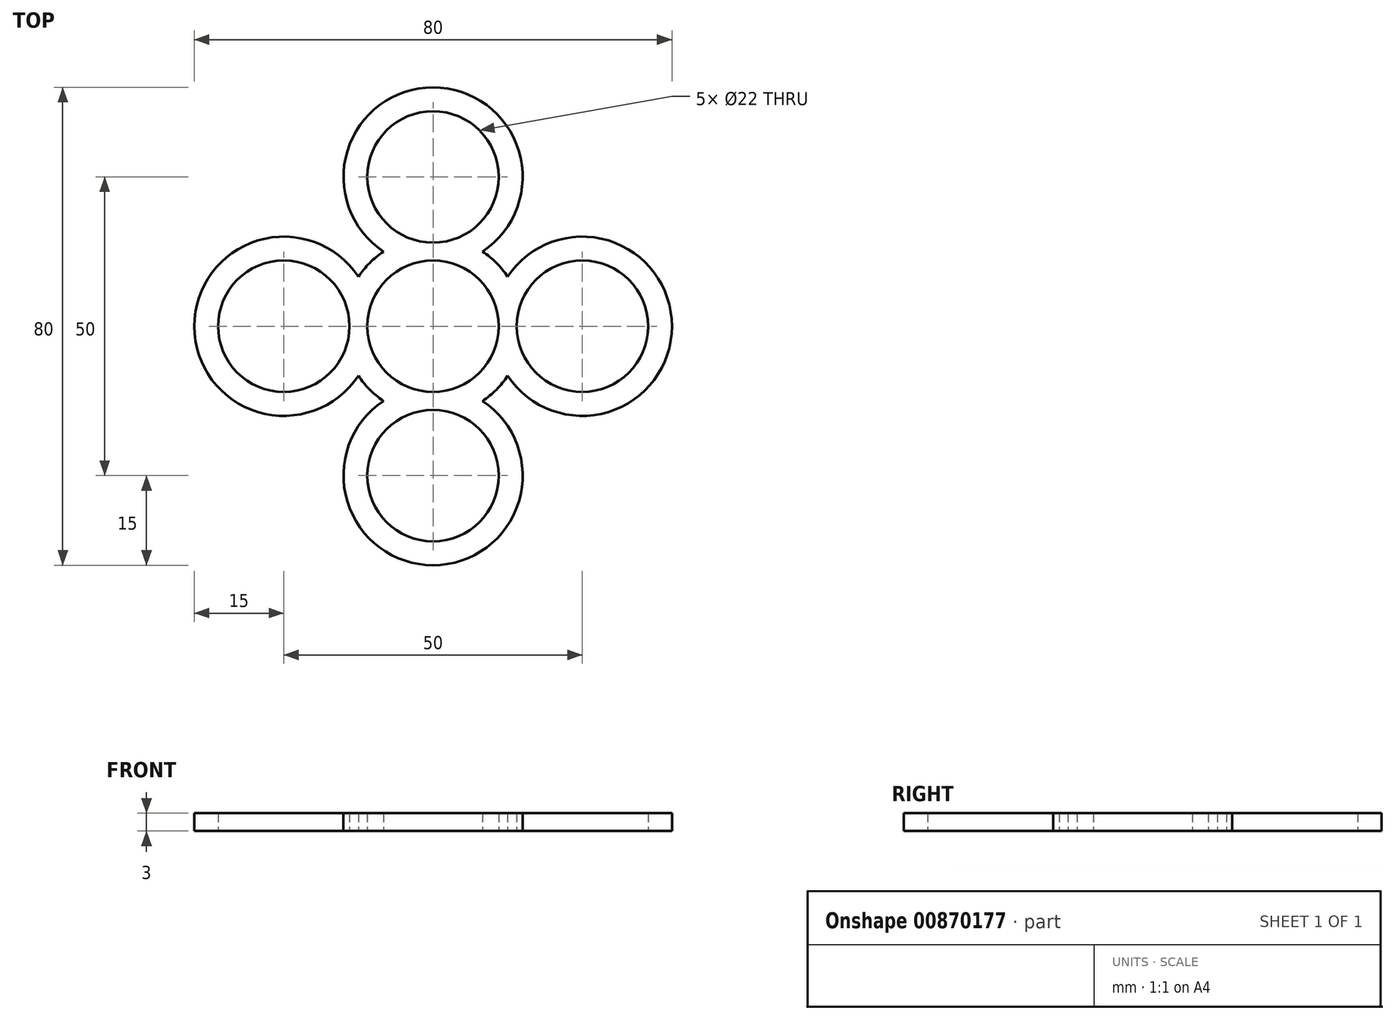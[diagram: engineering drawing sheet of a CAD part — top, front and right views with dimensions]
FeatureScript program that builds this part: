
annotation { "Feature Type Name" : "Feature", "Feature Type Description" : "" }
export const myFeature = defineFeature(function(context is Context, id is Id, definition is map)
    precondition{}
    {
        {
            var Q0;
            Q0=qCreatedBy(makeId("Top.planeOp"),FACE);
            var sketch = newSketch(context, id + "F0", { "sketchPlane" : qUnion([Q0])});
            skCircle(sketch, "E0", {"center": v(0, 0) * mm, "radius": 11 * mm});
            skArc(sketch, "E1", {"start": v(-12.5, -8.3) * mm, "mid": v(-10.6, -10.6) * mm, "end": v(-8.3, -12.5) * mm});
            skLineSegment(sketch, "E2", {"start": v(-10, 0) * mm, "end": v(-11, 0) * mm});
            skCircle(sketch, "E3", {"center": v(-25, 0) * mm, "radius": 11 * mm});
            skArc(sketch, "E4", {"start": v(-12.5, 8.3) * mm, "mid": v(-40, 0) * mm, "end": v(-12.5, -8.3) * mm});
            skLineSegment(sketch, "E5", {"start": v(0, 10) * mm, "end": v(0, 15) * mm});
            skCircle(sketch, "E6", {"center": v(0, 25) * mm, "radius": 11 * mm});
            skArc(sketch, "E7", {"start": v(8.3, 12.5) * mm, "mid": v(0, 40) * mm, "end": v(-8.3, 12.5) * mm});
            skLineSegment(sketch, "E8", {"start": v(0, -10) * mm, "end": v(0, -15) * mm});
            skCircle(sketch, "E9", {"center": v(0, -25) * mm, "radius": 11 * mm});
            skArc(sketch, "E10", {"start": v(-8.3, -12.5) * mm, "mid": v(0, -40) * mm, "end": v(8.3, -12.5) * mm});
            skArc(sketch, "E11.trimOffspring", {"start": v(8.3, -12.5) * mm, "mid": v(10.6, -10.6) * mm, "end": v(12.5, -8.3) * mm});
            skArc(sketch, "E12.trimOffspring", {"start": v(-8.3, 12.5) * mm, "mid": v(-10.6, 10.6) * mm, "end": v(-12.5, 8.3) * mm});
            skCircle(sketch, "E13", {"center": v(25, 0) * mm, "radius": 11 * mm});
            skArc(sketch, "E14", {"start": v(12.5, -8.3) * mm, "mid": v(40, 0) * mm, "end": v(12.5, 8.3) * mm});
            skArc(sketch, "E15.trimOffspring", {"start": v(12.5, 8.3) * mm, "mid": v(10.6, 10.6) * mm, "end": v(8.3, 12.5) * mm});
            skLineSegment(sketch, "E16.trimOffspring", {"start": v(-14, 0) * mm, "end": v(-15, 0) * mm});
            skSolve(sketch);
        }
        {
            var Q0;
            Q0=qSketchRegion(id+"F0",true);
            extrude(context, id + "F1", {"entities" : qUnion([Q0]), "depth" : 3 * mm, "offsetDistance" : 25.4 * mm});
        }
    });
